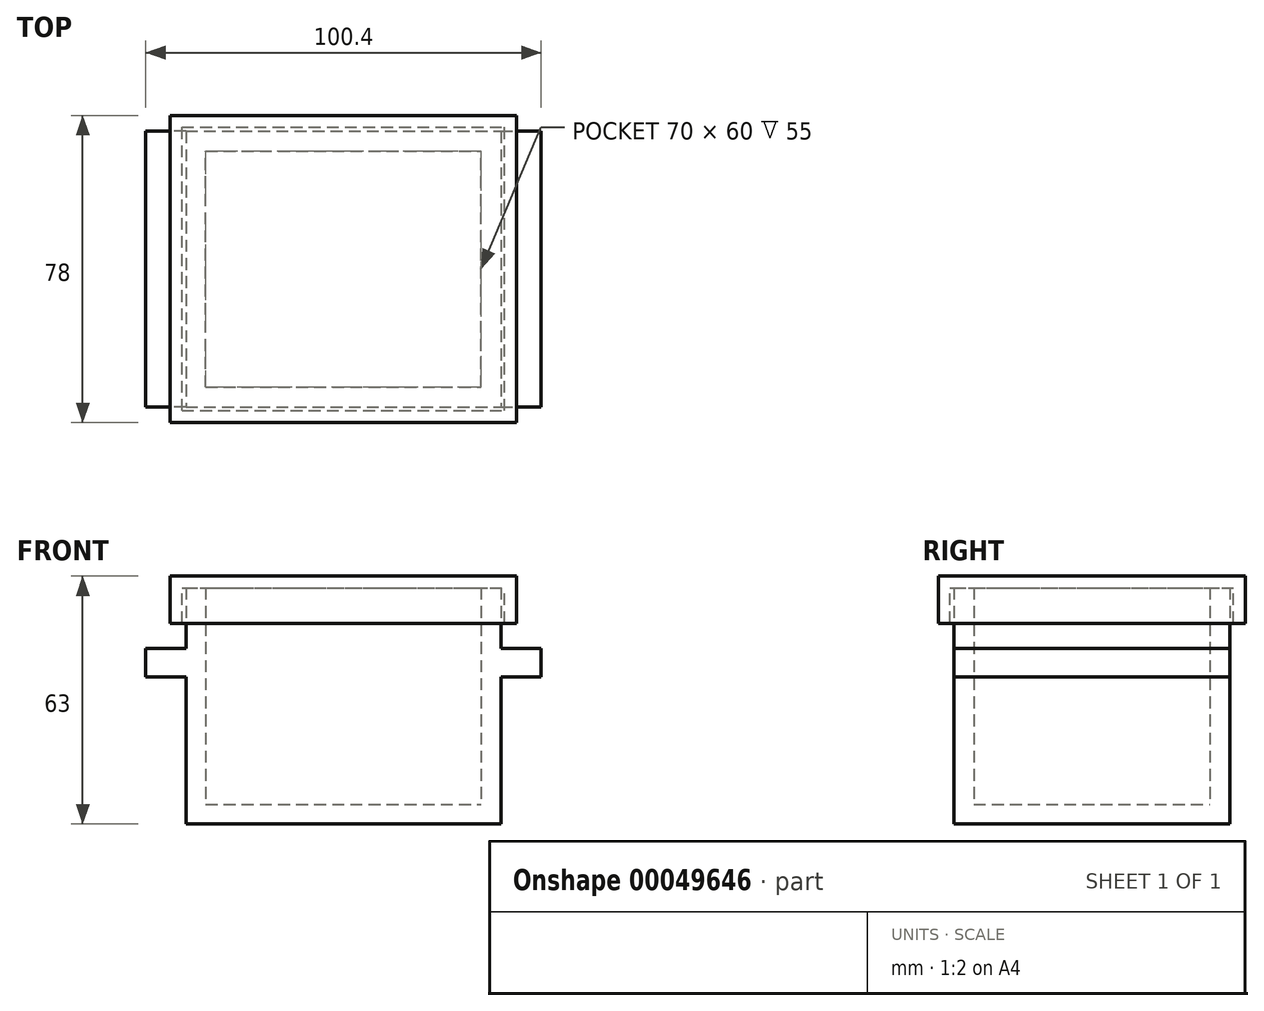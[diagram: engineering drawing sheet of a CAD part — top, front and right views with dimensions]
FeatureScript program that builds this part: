
annotation { "Feature Type Name" : "Feature", "Feature Type Description" : "" }
export const myFeature = defineFeature(function(context is Context, id is Id, definition is map)
    precondition{}
    {
        {
            var Q0;
            Q0=qCreatedBy(makeId("Top.planeOp"),FACE);
            var sketch = newSketch(context, id + "F0", { "sketchPlane" : qUnion([Q0])});
            skLineSegment(sketch, "E0.bottom", {"start": v(0, 0) * mm, "end": v(80, 0) * mm});
            skLineSegment(sketch, "E0.top", {"start": v(0, 70) * mm, "end": v(80, 70) * mm});
            skLineSegment(sketch, "E0.left", {"start": v(0, 0) * mm, "end": v(0, 70) * mm});
            skLineSegment(sketch, "E0.right", {"start": v(80, 0) * mm, "end": v(80, 70) * mm});
            skSolve(sketch);
        }
        {
            var Q0;
            Q0=makeQuery(id+"F0.imprint","IMPRINT",FACE,{"disambiguationData":[TD([[makeQuery(id+"F0.imprint","IMPRINT",EDGE,{"derivedFrom":sQuery(id+"F0.wireOp",EDGE,"E0.bottom")}),1.0]])]});
            extrude(context, id + "F1", {"entities" : qUnion([Q0]), "depth" : 60 * mm});
        }
        {
            var Q0;
            Q0=makeQuery(id+"F1.opExtrude","CAP_FACE",FACE,{"disambiguationData":[OSD([sQuery(id+"F0.wireOp",EDGE,"E0.bottom"),sQuery(id+"F0.wireOp",EDGE,"E0.top"),sQuery(id+"F0.wireOp",EDGE,"E0.left"),sQuery(id+"F0.wireOp",EDGE,"E0.right")])],"isStart":false});
            shell(context, id + "F2", {"entities" : qUnion([Q0]), "thickness" : 5 * mm});
        }
        {
            var Q0;
            Q0=makeQuery(id+"F1.opExtrude","CAP_FACE",FACE,{"disambiguationData":[OSD([sQuery(id+"F0.wireOp",EDGE,"E0.bottom"),sQuery(id+"F0.wireOp",EDGE,"E0.top"),sQuery(id+"F0.wireOp",EDGE,"E0.left"),sQuery(id+"F0.wireOp",EDGE,"E0.right")])],"isStart":false});
            cPlane(context, id + "F3", {"entities" : qUnion([Q0]), "cplaneType" : CPlaneType.OFFSET, "offset" : 3 * mm, "width" : 150 * mm, "height" : 150 * mm});
        }
        {
            var Q0;
            Q0=qCreatedBy(id+"F3.planeOp",FACE);
            var sketch = newSketch(context, id + "F4", { "sketchPlane" : qUnion([Q0])});
            skLineSegment(sketch, "E1.0", {"start": v(84, -4) * mm, "end": v(84, 74) * mm});
            skLineSegment(sketch, "E1.1", {"start": v(-4, -4) * mm, "end": v(84, -4) * mm});
            skLineSegment(sketch, "E1.2", {"start": v(-4, -4) * mm, "end": v(-4, 74) * mm});
            skLineSegment(sketch, "E1.3", {"start": v(-4, 74) * mm, "end": v(84, 74) * mm});
            skSolve(sketch);
        }
        {
            var Q0;
            Q0=makeQuery(id+"F4.imprint","IMPRINT",FACE,{"disambiguationData":[TD([[makeQuery(id+"F4.imprint","IMPRINT",EDGE,{"derivedFrom":sQuery(id+"F4.wireOp",EDGE,"E1.0")}),1.0]])]});
            var Q1;
            {var subQ0=sQuery(id+"F0.wireOp",EDGE,"E0.bottom");Q1=makeQuery(id+"F4.imprint","IMPRINT",FACE,{"disambiguationData":[TD([[makeQuery(id+"F4.imprint","IMPRINT",EDGE,{"derivedFrom":makeQuery(id+"F2.opShell","OFFSET_EDGE",EDGE,{"disambiguationData":[OSD([subQ0]),TDD([makeQuery(id+"F1.opExtrude","CAP_EDGE",EDGE,{"disambiguationData":[OSD([subQ0])],"isStart":false})])]})}),1.0]])]});}
            extrude(context, id + "F5", {"entities" : qUnion([Q0, Q1]), "oppositeDirection" : true, "depth" : 12 * mm});
        }
        {
            var Q0;
            Q0=makeQuery(id+"F5.opExtrude","CAP_FACE",FACE,{"disambiguationData":[OSD([sQuery(id+"F4.wireOp",EDGE,"E1.0"),sQuery(id+"F4.wireOp",EDGE,"E1.1"),sQuery(id+"F4.wireOp",EDGE,"E1.2"),sQuery(id+"F4.wireOp",EDGE,"E1.3")])],"isStart":false});
            shell(context, id + "F6", {"entities" : qUnion([Q0]), "thickness" : 3 * mm});
        }
        {
            var Q0;
            Q0=makeQuery(id+"F1.opExtrude","SWEPT_FACE",FACE,{"disambiguationData":[OSD([sQuery(id+"F0.wireOp",EDGE,"E0.bottom")])]});
            var sketch = newSketch(context, id + "F7", { "sketchPlane" : qUnion([Q0])});
            skLineSegment(sketch, "E2", {"start": v(0, 44.6) * mm, "end": v(-10.2, 44.6) * mm});
            skLineSegment(sketch, "E3", {"start": v(0, 44.6) * mm, "end": v(0, 37.4) * mm});
            skLineSegment(sketch, "E4", {"start": v(0, 37.4) * mm, "end": v(-10.2, 37.4) * mm});
            skLineSegment(sketch, "E5", {"start": v(-10.2, 37.4) * mm, "end": v(-10.2, 44.6) * mm});
            skLineSegment(sketch, "E6", {"start": v(40, 0) * mm, "end": v(40, 60) * mm, "construction": true});
            skLineSegment(sketch, "E7.MirrorCS", {"start": v(80, 44.6) * mm, "end": v(90.2, 44.6) * mm});
            skLineSegment(sketch, "E8.MirrorCS", {"start": v(90.2, 37.4) * mm, "end": v(90.2, 44.6) * mm});
            skLineSegment(sketch, "E9.MirrorCS", {"start": v(80, 37.4) * mm, "end": v(90.2, 37.4) * mm});
            skLineSegment(sketch, "E10.MirrorCS", {"start": v(80, 44.6) * mm, "end": v(80, 37.4) * mm});
            skSolve(sketch);
        }
        {
            var Q0;
            Q0=makeQuery(id+"F7.imprint","IMPRINT",FACE,{"disambiguationData":[TD([[makeQuery(id+"F7.imprint","IMPRINT",EDGE,{"derivedFrom":sQuery(id+"F7.wireOp",EDGE,"E2")}),1.0]])]});
            var Q1;
            Q1=makeQuery(id+"F7.imprint","IMPRINT",FACE,{"disambiguationData":[TD([[makeQuery(id+"F7.imprint","IMPRINT",EDGE,{"derivedFrom":sQuery(id+"F7.wireOp",EDGE,"E7.MirrorCS")}),-1.0]])]});
            var Q2;
            Q2=makeQuery(id+"F1.opExtrude","SWEPT_FACE",FACE,{"disambiguationData":[OSD([sQuery(id+"F0.wireOp",EDGE,"E0.top")])]});
            extrude(context, id + "F8", {"entities" : qUnion([Q0, Q1]), "operationType" : NewBodyOperationType.ADD, "endBound" : BoundingType.UP_TO_SURFACE, "oppositeDirection" : true, "endBoundEntityFace" : qUnion([Q2]), "depth" : 25 * mm});
        }
    });
